# Revit family: UM396E Banco Trau
name_source: partatom
category: Mobiliario
units: mm (PartAtom-declared; Revit-internal decimal feet)

## family parameters
Compartido = No
Corte con vacíos al cargar = No
Número OmniClass = 23.40.20.00
Punto de cálculo de habitación = No
Se basa en plano de trabajo = No
Siempre vertical = Sí
Título OmniClass = General Furniture and Specialties

## types (1)
- UM396E Banco Trau
    Acabado banco = Ferrus, proceso protector del hierro, que garantiza una óptima resistencia a la corrosión
    Accessibilidad = Sí
    Altura asiento = 510 mm  [stored 1.67323 ft]
    Altura total = 510 mm  [stored 1.67323 ft]
    Ancho = 630 mm  [stored 2.06693 ft]
    Comentarios de tipo = Acero galvanizado con tratamiento Ferrus, proceso protector del hierro, que garantiza una óptima resistencia a la corrosión. Pies
imprimación epoxi y pintura poliéster en polvo color negro forja y asiento imprimación epoxi y pintura poliéster en polvo color gris
plata RAL 9006.
    Fabricante = BENITO
    Ficha tecnica = http://www.benito.com
    Instalación = Tornillos de fijación al suelo de M10 según superficie y proyecto.No suministrados
    Largo = 2000 mm  [stored 6.56168 ft]
    Material banco = Acero galvanizado.
    Modelo = Banco Trau
    Referencia = UM396E
    URL = http://www.benito.com
    URL Producto = http://www.benito.com

note: [stored X ft] marks values corroborated as IEEE doubles in the binary element streams (Revit-internal decimal feet)

## geometry (parser evidence)
native form markers: Blend x4
no freeform markers — native parametric forms only
